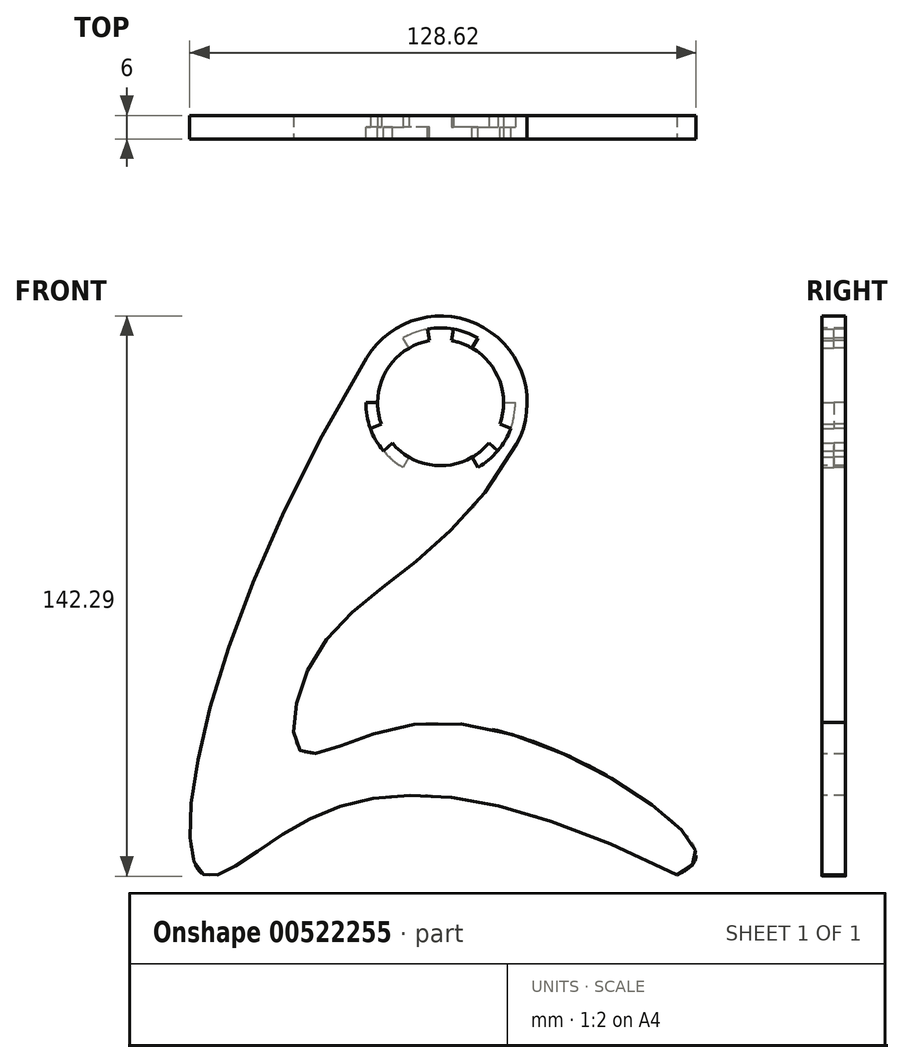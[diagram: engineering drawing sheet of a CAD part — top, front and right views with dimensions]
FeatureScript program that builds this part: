
annotation { "Feature Type Name" : "Feature", "Feature Type Description" : "" }
export const myFeature = defineFeature(function(context is Context, id is Id, definition is map)
    precondition{}
    {
        {
            var Q0;
            Q0=qCreatedBy(makeId("Front.planeOp"),FACE);
            var sketch = newSketch(context, id + "F0", { "sketchPlane" : qUnion([Q0])});
            skPoint(sketch, "E0", {"position": v(0, 0) * mm});
            skPoint(sketch, "E1", {"position": v(0, 120) * mm});
            skCircle(sketch, "E2", {"center": v(0, 120) * mm, "radius": 16 * mm});
            skCircle(sketch, "E3", {"center": v(0, 120) * mm, "radius": 22 * mm});
            skLineSegment(sketch, "E4", {"start": v(0, 0) * mm, "end": v(-60, 0) * mm, "construction": true});
            skLineSegment(sketch, "E5", {"start": v(0, 0) * mm, "end": v(60, 0) * mm, "construction": true});
            skLineSegment(sketch, "E6", {"start": v(0, 0) * mm, "end": v(0, 120) * mm, "construction": true});
            skFitSpline(sketch, "E7", {"points": [v(60, 0) * mm, v(-36.62, 12.42) * mm, v(-60, 0) * mm, v(-18.83, 131.37) * mm], "startDerivative": vector(-411.27, 206.3) * mm, "endDerivative": vector(280.6, 464.64) * mm});
            skFitSpline(sketch, "E8", {"points": [v(19.3, 109.45) * mm, v(-30.52, 57.7) * mm, v(-35.34, 31.37) * mm, v(0, 38.76) * mm, v(64.54, 6.78) * mm, v(60, 0) * mm], "startDerivative": vector(-175.02, -320.3) * mm, "endDerivative": vector(-116.62, -55.2) * mm});
            skText(sketch, "E9", { "text": "SECTION 31", "fontName": "Arimo-Regular.ttf"});
            skEllipticalArc(sketch, "E10", {});
            skEllipticalArc(sketch, "E11", {});
            skLineSegment(sketch, "E12", {"start": v(-40.76, 83.27) * mm, "end": v(-41.08, 82.59) * mm});
            skLineSegment(sketch, "E13", {"start": v(-38.21, 80.66) * mm, "end": v(-38.44, 80.18) * mm});
            skLineSegment(sketch, "E14.bottom", {"start": v(-43.25, 77.14) * mm, "end": v(-39.87, 84.4) * mm});
            skLineSegment(sketch, "E14.top", {"start": v(-42.7, 76.89) * mm, "end": v(-39.33, 84.14) * mm});
            skLineSegment(sketch, "E14.left", {"start": v(-43.25, 77.14) * mm, "end": v(-42.7, 76.89) * mm});
            skLineSegment(sketch, "E14.right", {"start": v(-39.87, 84.4) * mm, "end": v(-39.33, 84.14) * mm});
            skLineSegment(sketch, "E15.0.1.0", {"start": v(-41.98, 75.9) * mm, "end": v(-38.6, 83.15) * mm});
            skLineSegment(sketch, "E15.0.1.1", {"start": v(-42.52, 76.15) * mm, "end": v(-39.14, 83.4) * mm});
            skLineSegment(sketch, "E15.0.1.2", {"start": v(-42.52, 76.15) * mm, "end": v(-41.98, 75.9) * mm});
            skLineSegment(sketch, "E15.0.1.3", {"start": v(-39.14, 83.4) * mm, "end": v(-38.6, 83.15) * mm});
            skLineSegment(sketch, "E15.0.2.0", {"start": v(-41.25, 74.9) * mm, "end": v(-37.87, 82.16) * mm});
            skLineSegment(sketch, "E15.0.2.1", {"start": v(-41.8, 75.16) * mm, "end": v(-38.41, 82.41) * mm});
            skLineSegment(sketch, "E15.0.2.2", {"start": v(-41.8, 75.16) * mm, "end": v(-41.25, 74.9) * mm});
            skLineSegment(sketch, "E15.0.2.3", {"start": v(-38.41, 82.41) * mm, "end": v(-37.87, 82.16) * mm});
            skLineSegment(sketch, "E15.direction2", {"start": v(-42.7, 76.89) * mm, "end": v(-41.98, 75.9) * mm, "construction": true});
            skLineSegment(sketch, "E16", {"start": v(-32.37, 77.02) * mm, "end": v(-29.73, 82.67) * mm});
            skArc(sketch, "E17", {"start": v(9.5, 136.45) * mm, "mid": v(0, 139) * mm, "end": v(-9.5, 136.45) * mm});
            skLineSegment(sketch, "E18", {"start": v(0, 120) * mm, "end": v(0, 136) * mm, "construction": true});
            skLineSegment(sketch, "E19", {"start": v(0, 120) * mm, "end": v(8, 133.86) * mm, "construction": true});
            skLineSegment(sketch, "E20", {"start": v(8, 133.86) * mm, "end": v(9.5, 136.45) * mm});
            skLineSegment(sketch, "E21", {"start": v(0, 120) * mm, "end": v(-2.78, 135.76) * mm, "construction": true});
            skLineSegment(sketch, "E22", {"start": v(-2.78, 135.76) * mm, "end": v(-3.3, 138.71) * mm});
            skLineSegment(sketch, "E23", {"start": v(0, 136) * mm, "end": v(0, 139) * mm});
            skLineSegment(sketch, "E24", {"start": v(0, 120) * mm, "end": v(2.78, 135.76) * mm, "construction": true});
            skLineSegment(sketch, "E25", {"start": v(2.78, 135.76) * mm, "end": v(3.3, 138.71) * mm});
            skLineSegment(sketch, "E26", {"start": v(0, 120) * mm, "end": v(-8, 133.86) * mm, "construction": true});
            skLineSegment(sketch, "E27", {"start": v(-8, 133.86) * mm, "end": v(-9.5, 136.45) * mm});
            skLineSegment(sketch, "E28.1.0", {"start": v(-8, 106.14) * mm, "end": v(-9.5, 103.55) * mm});
            skLineSegment(sketch, "E28.1.1", {"start": v(-12.26, 109.72) * mm, "end": v(-14.55, 107.79) * mm});
            skLineSegment(sketch, "E28.1.2", {"start": v(-13.86, 112) * mm, "end": v(-16.45, 110.5) * mm});
            skLineSegment(sketch, "E28.1.3", {"start": v(-15.04, 114.53) * mm, "end": v(-17.85, 113.5) * mm});
            skLineSegment(sketch, "E28.1.4", {"start": v(-16, 120) * mm, "end": v(-19, 120) * mm});
            skArc(sketch, "E28.1.5", {"start": v(-19, 120) * mm, "mid": v(-16.45, 110.5) * mm, "end": v(-9.5, 103.55) * mm});
            skLineSegment(sketch, "E28.2.0", {"start": v(16, 120) * mm, "end": v(19, 120) * mm});
            skLineSegment(sketch, "E28.2.1", {"start": v(15.04, 114.53) * mm, "end": v(17.85, 113.5) * mm});
            skLineSegment(sketch, "E28.2.2", {"start": v(13.86, 112) * mm, "end": v(16.45, 110.5) * mm});
            skLineSegment(sketch, "E28.2.3", {"start": v(12.26, 109.72) * mm, "end": v(14.55, 107.79) * mm});
            skLineSegment(sketch, "E28.2.4", {"start": v(8, 106.14) * mm, "end": v(9.5, 103.55) * mm});
            skArc(sketch, "E28.2.5", {"start": v(9.5, 103.55) * mm, "mid": v(16.45, 110.5) * mm, "end": v(19, 120) * mm});
            skLineSegment(sketch, "E29", {"start": v(-49.15, 57.03) * mm, "end": v(-46.02, 74.76) * mm});
            skLineSegment(sketch, "E30", {"start": v(-46.02, 74.76) * mm, "end": v(-41.53, 86.03) * mm});
            skLineSegment(sketch, "E31", {"start": v(-41.53, 86.03) * mm, "end": v(-24.94, 106.73) * mm});
            skLineSegment(sketch, "E32", {"start": v(-24.94, 106.73) * mm, "end": v(-17.02, 102.62) * mm});
            skLineSegment(sketch, "E33", {"start": v(-17.02, 102.62) * mm, "end": v(-39.55, 53.3) * mm});
            skLineSegment(sketch, "E34", {"start": v(-39.55, 53.3) * mm, "end": v(-49.15, 57.03) * mm});
            const initialGuessF0  = {"E9": [-0.04018, 0.05677, 0.42262, 0.9063, 0.0061], "E10": [-0.03856819608204748, 0.08323794192713017, -0.598780962764818, 0.8009128283592652, 0.0035, 0.0025, 2.378483096717644, 1.286216884327917], "E11": [-0.038915451380973326, 0.08284818077287295, -0.5987809627648178, 0.8009128283592655, 0.0025, 0.0015, 2.6230590624912136, 0.9557211492362822]};
            skSetInitialGuess(sketch, initialGuessF0);
            skSolve(sketch);
        }
        {
            var Q0;
            {var subQ0=sQuery(id+"F0.wireOp",EDGE,"E20");Q0=makeQuery(id+"F0.imprint","IMPRINT",FACE,{"disambiguationData":[TD([[makeQuery(id+"F0.imprint","IMPRINT",EDGE,{"derivedFrom":subQ0}),1.0]])]});}
            var Q1;
            {var subQ15=sQuery(id+"F0.wireOp",EDGE,"E20");Q1=makeQuery(id+"F0.imprint","IMPRINT",FACE,{"disambiguationData":[TD([[makeQuery(id+"F0.imprint","IMPRINT",EDGE,{"derivedFrom":subQ15}),-1.0]])]});}
            var Q2;
            {var subQ12=sQuery(id+"F0.wireOp",EDGE,"E7");Q2=makeQuery(id+"F0.imprint","IMPRINT",FACE,{"disambiguationData":[TD([[makeQuery(id+"F0.imprint","IMPRINT",EDGE,{"derivedFrom":subQ12}),-1.0]])]});}
            var Q3;
            Q3=makeQuery(id+"F0.imprint","IMPRINT",FACE,{"disambiguationData":[TD([[makeQuery(id+"F0.imprint","IMPRINT",EDGE,{"derivedFrom":sQuery(id+"F0.wireOp",EDGE,"E9.sketch_text.stroke-108")}),-1.0]])]});
            var Q4;
            Q4=makeQuery(id+"F0.imprint","IMPRINT",FACE,{"disambiguationData":[TD([[makeQuery(id+"F0.imprint","IMPRINT",EDGE,{"derivedFrom":sQuery(id+"F0.wireOp",EDGE,"E9.sketch_text.stroke-95")}),-1.0]])]});
            var Q5;
            Q5=makeQuery(id+"F0.imprint","IMPRINT",FACE,{"disambiguationData":[TD([[makeQuery(id+"F0.imprint","IMPRINT",EDGE,{"derivedFrom":sQuery(id+"F0.wireOp",EDGE,"E9.sketch_text.stroke-34")}),-1.0]])]});
            var Q6;
            Q6=makeQuery(id+"F0.imprint","IMPRINT",FACE,{"disambiguationData":[TD([[makeQuery(id+"F0.imprint","IMPRINT",EDGE,{"derivedFrom":sQuery(id+"F0.wireOp",EDGE,"E9.sketch_text.stroke-137")}),-1.0]])]});
            var Q7;
            Q7=makeQuery(id+"F0.imprint","IMPRINT",FACE,{"disambiguationData":[TD([[makeQuery(id+"F0.imprint","IMPRINT",EDGE,{"derivedFrom":sQuery(id+"F0.wireOp",EDGE,"E9.sketch_text.stroke-87")}),1.0]])]});
            var Q8;
            Q8=makeQuery(id+"F0.imprint","IMPRINT",FACE,{"disambiguationData":[TD([[makeQuery(id+"F0.imprint","IMPRINT",EDGE,{"derivedFrom":sQuery(id+"F0.wireOp",EDGE,"E9.sketch_text.stroke-64")}),-1.0]])]});
            var Q9;
            Q9=makeQuery(id+"F0.imprint","IMPRINT",FACE,{"disambiguationData":[TD([[makeQuery(id+"F0.imprint","IMPRINT",EDGE,{"derivedFrom":sQuery(id+"F0.wireOp",EDGE,"E9.sketch_text.stroke-0")}),-1.0]])]});
            var Q10;
            Q10=makeQuery(id+"F0.imprint","IMPRINT",FACE,{"disambiguationData":[TD([[makeQuery(id+"F0.imprint","IMPRINT",EDGE,{"derivedFrom":sQuery(id+"F0.wireOp",EDGE,"E9.sketch_text.stroke-76")}),-1.0]])]});
            var Q11;
            Q11=makeQuery(id+"F0.imprint","IMPRINT",FACE,{"disambiguationData":[TD([[makeQuery(id+"F0.imprint","IMPRINT",EDGE,{"derivedFrom":sQuery(id+"F0.wireOp",EDGE,"E9.sketch_text.stroke-46")}),-1.0]])]});
            var Q12;
            {var subQ0=sQuery(id+"F0.wireOp",EDGE,"E9.sketch_text.stroke-73");Q12=makeQuery(id+"F0.imprint","IMPRINT",FACE,{"disambiguationData":[TD([[makeQuery(id+"F0.imprint","IMPRINT",EDGE,{"derivedFrom":subQ0}),-1.0]])]});}
            var Q13;
            {var subQ0=sQuery(id+"F0.wireOp",EDGE,"E9.sketch_text.stroke-75");Q13=makeQuery(id+"F0.imprint","IMPRINT",FACE,{"disambiguationData":[TD([[makeQuery(id+"F0.imprint","IMPRINT",EDGE,{"derivedFrom":subQ0}),-1.0]])]});}
            var Q14;
            Q14=makeQuery(id+"F0.imprint","IMPRINT",FACE,{"disambiguationData":[TD([[makeQuery(id+"F0.imprint","IMPRINT",EDGE,{"derivedFrom":sQuery(id+"F0.wireOp",EDGE,"E15.0.2.0")}),1.0]])]});
            var Q15;
            Q15=makeQuery(id+"F0.imprint","IMPRINT",FACE,{"disambiguationData":[TD([[makeQuery(id+"F0.imprint","IMPRINT",EDGE,{"derivedFrom":sQuery(id+"F0.wireOp",EDGE,"E14.bottom")}),-1.0]])]});
            var Q16;
            Q16=makeQuery(id+"F0.imprint","IMPRINT",FACE,{"disambiguationData":[TD([[makeQuery(id+"F0.imprint","IMPRINT",EDGE,{"derivedFrom":sQuery(id+"F0.wireOp",EDGE,"E10")}),1.0]])]});
            var Q17;
            Q17=makeQuery(id+"F0.imprint","IMPRINT",FACE,{"disambiguationData":[TD([[makeQuery(id+"F0.imprint","IMPRINT",EDGE,{"derivedFrom":sQuery(id+"F0.wireOp",EDGE,"E15.0.1.0")}),1.0]])]});
            var Q18;
            {var subQ0=sQuery(id+"F0.wireOp",EDGE,"E28.1.3");Q18=makeQuery(id+"F0.imprint","IMPRINT",FACE,{"disambiguationData":[TD([[makeQuery(id+"F0.imprint","IMPRINT",EDGE,{"derivedFrom":subQ0}),-1.0]])]});}
            var Q19;
            {var subQ0=sQuery(id+"F0.wireOp",EDGE,"E28.2.3");Q19=makeQuery(id+"F0.imprint","IMPRINT",FACE,{"disambiguationData":[TD([[makeQuery(id+"F0.imprint","IMPRINT",EDGE,{"derivedFrom":subQ0}),-1.0]])]});}
            var Q20;
            Q20=makeQuery(id+"F0.imprint","IMPRINT",FACE,{"disambiguationData":[TD([[makeQuery(id+"F0.imprint","IMPRINT",EDGE,{"derivedFrom":sQuery(id+"F0.wireOp",EDGE,"E9.sketch_text.stroke-0")}),1.0]])]});
            extrude(context, id + "F1", {"entities" : qUnion([Q0, Q1, Q2, Q3, Q4, Q5, Q6, Q7, Q8, Q9, Q10, Q11, Q12, Q13, Q14, Q15, Q16, Q17, Q18, Q19, Q20]), "oppositeDirection" : true, "depth" : 3 * mm, "offsetDistance" : 25 * mm});
        }
        {
            var Q0;
            {var subQ1=sQuery(id+"F0.wireOp",EDGE,"E7");Q0=makeQuery(id+"F0.imprint","IMPRINT",FACE,{"disambiguationData":[TD([[makeQuery(id+"F0.imprint","IMPRINT",EDGE,{"derivedFrom":subQ1}),-1.0]])]});}
            var Q1;
            {var subQ15=sQuery(id+"F0.wireOp",EDGE,"E20");Q1=makeQuery(id+"F0.imprint","IMPRINT",FACE,{"disambiguationData":[TD([[makeQuery(id+"F0.imprint","IMPRINT",EDGE,{"derivedFrom":subQ15}),-1.0]])]});}
            var Q2;
            {var subQ0=sQuery(id+"F0.wireOp",EDGE,"E22");Q2=makeQuery(id+"F0.imprint","IMPRINT",FACE,{"disambiguationData":[TD([[makeQuery(id+"F0.imprint","IMPRINT",EDGE,{"derivedFrom":subQ0}),1.0]])]});}
            var Q3;
            {var subQ0=sQuery(id+"F0.wireOp",EDGE,"E28.1.0");Q3=makeQuery(id+"F0.imprint","IMPRINT",FACE,{"disambiguationData":[TD([[makeQuery(id+"F0.imprint","IMPRINT",EDGE,{"derivedFrom":subQ0}),-1.0]])]});}
            var Q4;
            {var subQ0=sQuery(id+"F0.wireOp",EDGE,"E28.2.0");Q4=makeQuery(id+"F0.imprint","IMPRINT",FACE,{"disambiguationData":[TD([[makeQuery(id+"F0.imprint","IMPRINT",EDGE,{"derivedFrom":subQ0}),-1.0]])]});}
            var Q5;
            Q5=makeQuery(id+"F0.imprint","IMPRINT",FACE,{"disambiguationData":[TD([[makeQuery(id+"F0.imprint","IMPRINT",EDGE,{"derivedFrom":sQuery(id+"F0.wireOp",EDGE,"E9.sketch_text.stroke-108")}),-1.0]])]});
            var Q6;
            Q6=makeQuery(id+"F0.imprint","IMPRINT",FACE,{"disambiguationData":[TD([[makeQuery(id+"F0.imprint","IMPRINT",EDGE,{"derivedFrom":sQuery(id+"F0.wireOp",EDGE,"E9.sketch_text.stroke-137")}),-1.0]])]});
            var Q7;
            Q7=makeQuery(id+"F0.imprint","IMPRINT",FACE,{"disambiguationData":[TD([[makeQuery(id+"F0.imprint","IMPRINT",EDGE,{"derivedFrom":sQuery(id+"F0.wireOp",EDGE,"E9.sketch_text.stroke-95")}),-1.0]])]});
            var Q8;
            Q8=makeQuery(id+"F0.imprint","IMPRINT",FACE,{"disambiguationData":[TD([[makeQuery(id+"F0.imprint","IMPRINT",EDGE,{"derivedFrom":sQuery(id+"F0.wireOp",EDGE,"E9.sketch_text.stroke-76")}),-1.0]])]});
            var Q9;
            {var subQ0=sQuery(id+"F0.wireOp",EDGE,"E9.sketch_text.stroke-75");Q9=makeQuery(id+"F0.imprint","IMPRINT",FACE,{"disambiguationData":[TD([[makeQuery(id+"F0.imprint","IMPRINT",EDGE,{"derivedFrom":subQ0}),-1.0]])]});}
            var Q10;
            {var subQ0=sQuery(id+"F0.wireOp",EDGE,"E9.sketch_text.stroke-73");Q10=makeQuery(id+"F0.imprint","IMPRINT",FACE,{"disambiguationData":[TD([[makeQuery(id+"F0.imprint","IMPRINT",EDGE,{"derivedFrom":subQ0}),-1.0]])]});}
            var Q11;
            Q11=makeQuery(id+"F0.imprint","IMPRINT",FACE,{"disambiguationData":[TD([[makeQuery(id+"F0.imprint","IMPRINT",EDGE,{"derivedFrom":sQuery(id+"F0.wireOp",EDGE,"E9.sketch_text.stroke-64")}),-1.0]])]});
            var Q12;
            Q12=makeQuery(id+"F0.imprint","IMPRINT",FACE,{"disambiguationData":[TD([[makeQuery(id+"F0.imprint","IMPRINT",EDGE,{"derivedFrom":sQuery(id+"F0.wireOp",EDGE,"E9.sketch_text.stroke-46")}),-1.0]])]});
            var Q13;
            Q13=makeQuery(id+"F0.imprint","IMPRINT",FACE,{"disambiguationData":[TD([[makeQuery(id+"F0.imprint","IMPRINT",EDGE,{"derivedFrom":sQuery(id+"F0.wireOp",EDGE,"E9.sketch_text.stroke-34")}),-1.0]])]});
            var Q14;
            Q14=makeQuery(id+"F0.imprint","IMPRINT",FACE,{"disambiguationData":[TD([[makeQuery(id+"F0.imprint","IMPRINT",EDGE,{"derivedFrom":sQuery(id+"F0.wireOp",EDGE,"E9.sketch_text.stroke-0")}),-1.0]])]});
            var Q15;
            Q15=makeQuery(id+"F0.imprint","IMPRINT",FACE,{"disambiguationData":[TD([[makeQuery(id+"F0.imprint","IMPRINT",EDGE,{"derivedFrom":sQuery(id+"F0.wireOp",EDGE,"E15.0.2.0")}),1.0]])]});
            var Q16;
            Q16=makeQuery(id+"F0.imprint","IMPRINT",FACE,{"disambiguationData":[TD([[makeQuery(id+"F0.imprint","IMPRINT",EDGE,{"derivedFrom":sQuery(id+"F0.wireOp",EDGE,"E15.0.1.0")}),1.0]])]});
            var Q17;
            Q17=makeQuery(id+"F0.imprint","IMPRINT",FACE,{"disambiguationData":[TD([[makeQuery(id+"F0.imprint","IMPRINT",EDGE,{"derivedFrom":sQuery(id+"F0.wireOp",EDGE,"E14.bottom")}),-1.0]])]});
            var Q18;
            Q18=makeQuery(id+"F0.imprint","IMPRINT",FACE,{"disambiguationData":[TD([[makeQuery(id+"F0.imprint","IMPRINT",EDGE,{"derivedFrom":sQuery(id+"F0.wireOp",EDGE,"E10")}),1.0]])]});
            var Q19;
            Q19=makeQuery(id+"F0.imprint","IMPRINT",FACE,{"disambiguationData":[TD([[makeQuery(id+"F0.imprint","IMPRINT",EDGE,{"derivedFrom":sQuery(id+"F0.wireOp",EDGE,"E9.sketch_text.stroke-0")}),1.0]])]});
            var Q20;
            Q20=makeQuery(id+"F0.imprint","IMPRINT",FACE,{"disambiguationData":[TD([[makeQuery(id+"F0.imprint","IMPRINT",EDGE,{"derivedFrom":sQuery(id+"F0.wireOp",EDGE,"E9.sketch_text.stroke-87")}),1.0]])]});
            extrude(context, id + "F2", {"entities" : qUnion([Q0, Q1, Q2, Q3, Q4, Q5, Q6, Q7, Q8, Q9, Q10, Q11, Q12, Q13, Q14, Q15, Q16, Q17, Q18, Q19, Q20]), "operationType" : NewBodyOperationType.ADD, "depth" : 3 * mm, "offsetDistance" : 25 * mm});
        }
    });
